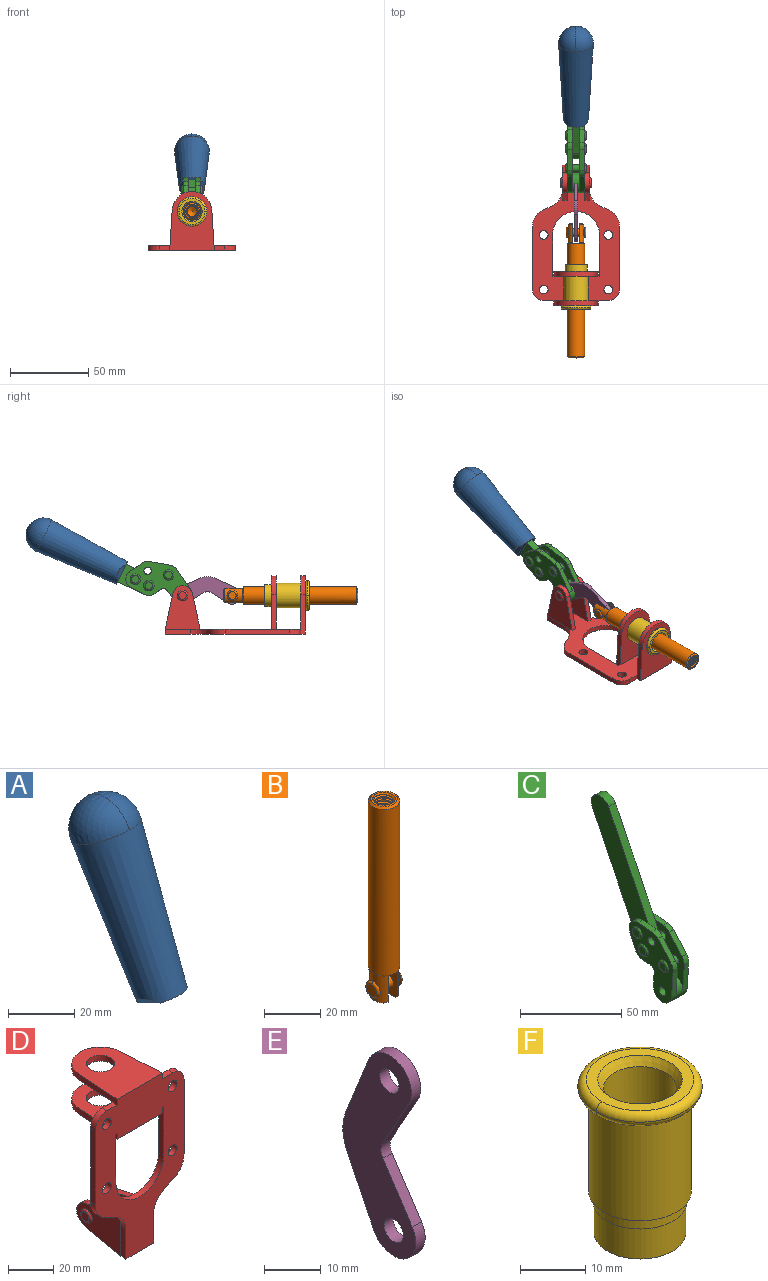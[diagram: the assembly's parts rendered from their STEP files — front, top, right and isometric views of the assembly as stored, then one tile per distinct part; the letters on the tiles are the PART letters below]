
ASSEMBLY  parts=6 mates=6
PART A: 11 faces, bbox 22.3x42.6x64.5 mm
  f0: sphere r=11.13mm, area 411.4mm2, adj f1,f8
  f1: cone r=11.11mm half-angle=3.3deg, axis (0,0.44,0.9), area 3251.8mm2, adj f0,f7,f8,f9,f10
  f2: cylinder r=6.16mm len=11.7mm, axis (1,0,0), area 89.5mm2, adj f3,f4,f5,f6
  f3: plane 60.23x36.75mm, normal (-1,0,0), area 763.6mm2, adj f2,f4,f6,f10
  f4: plane 51.37x25.05mm, normal (0,0.9,-0.44), area 264.2mm2, adj f2,f3,f5,f10
  f5: plane 60.23x36.75mm, normal (1,0,0), area 763.6mm2, adj f2,f4,f6,f10
  f6: plane 51.37x25.05mm, normal (0,-0.9,0.44), area 264.2mm2, adj f2,f3,f5,f10
  f7: plane 9.95x5.95mm, normal (0.71,-0.31,-0.64), area 25.8mm2, adj f1,f10
  f8: sphere r=11.13mm, area 411.4mm2, adj f0,f1
  f9: plane 9.95x5.95mm, normal (-0.71,-0.31,-0.64), area 25.8mm2, adj f1,f10
  f10: plane 14.27x11.38mm, normal (0,-0.44,-0.9), area 106.7mm2, adj f1,f3,f4,f5,f6,f7,f9
PART B: 48 faces, bbox 12.6x11.1x86.1 mm
  f0: torus R=2.41mm, axis (-1,0,0), area 15mm2, adj f30,f32,f34
  f1: torus R=2.41mm, axis (-1,0,0), area 15mm2, adj f29,f31,f33
  f2: cylinder r=5.54mm len=72.39mm, axis (0,0,1), area 2518.5mm2, adj f3,f4,f42,f43
  f3: cone r=5.54mm half-angle=45deg, axis (0,0,1), area 7.6mm2, adj f2,f5,f41
  f4: cone r=5.54mm half-angle=45deg, axis (0,0,-1), area 34.9mm2, adj f2,f39
  f5: cylinder r=5.08mm len=11.48mm, axis (0,0,1), area 108.3mm2, adj f3,f7,f8,f41
  f6: cylinder r=2.41mm len=4.83mm, axis (-1,0,0), area 71.2mm2, adj f40,f41
  f7: cylinder r=2.41mm len=4.83mm, axis (-1,0,0), area 7.6mm2, adj f5,f34
  f8: cone r=5.08mm half-angle=45deg, axis (0,0,1), area 10.6mm2, adj f5,f37,f41
  f9: cone r=3.98mm half-angle=45deg, axis (0,0,1), area 17.6mm2, adj f27,f39,f45,f46,f47
  f10: cylinder r=2.41mm len=4.83mm, axis (-1,0,0), area 7.6mm2, adj f33,f38
  f11: cylinder r=3.2mm len=6.4mm, axis (0,0,1), area 78.4mm2, adj f12,f28,f44,f45,f47
  f12: cylinder r=3.2mm len=6.4mm, axis (0,0,1), area 10.5mm2, adj f11,f13,f45,f47
  f13: cylinder r=3.2mm len=6.4mm, axis (0,0,1), area 10.5mm2, adj f12,f14,f45,f47
  f14: cylinder r=3.2mm len=6.4mm, axis (0,0,1), area 10.5mm2, adj f13,f15,f45,f47
  f15: cylinder r=3.2mm len=6.4mm, axis (0,0,1), area 10.5mm2, adj f14,f16,f45,f47
  f16: cylinder r=3.2mm len=6.4mm, axis (0,0,1), area 10.5mm2, adj f15,f17,f45,f47
  f17: cylinder r=3.2mm len=6.4mm, axis (0,0,1), area 10.5mm2, adj f16,f18,f45,f47
  f18: cylinder r=3.2mm len=6.4mm, axis (0,0,1), area 10.5mm2, adj f17,f19,f45,f47
  f19: cylinder r=3.2mm len=6.4mm, axis (0,0,1), area 10.5mm2, adj f18,f20,f45,f47
  f20: cylinder r=3.2mm len=6.4mm, axis (0,0,1), area 10.5mm2, adj f19,f21,f45,f47
  f21: cylinder r=3.2mm len=6.4mm, axis (0,0,1), area 10.5mm2, adj f20,f22,f45,f47
  f22: cylinder r=3.2mm len=6.4mm, axis (0,0,1), area 10.5mm2, adj f21,f23,f45,f47
  f23: cylinder r=3.2mm len=6.4mm, axis (0,0,1), area 10.5mm2, adj f22,f24,f45,f47
  f24: cylinder r=3.2mm len=6.4mm, axis (0,0,1), area 10.5mm2, adj f23,f25,f45,f47
  f25: cylinder r=3.2mm len=6.4mm, axis (0,0,1), area 10.5mm2, adj f24,f26,f45,f47
  f26: cylinder r=3.2mm len=6.4mm, axis (0,0,1), area 10.5mm2, adj f25,f27,f45,f47
  f27: cylinder r=3.2mm len=6.4mm, axis (0,0,1), area 7.4mm2, adj f9,f26,f45,f47
  f28: cone r=3.2mm half-angle=60deg, axis (0,0,1), area 37.2mm2, adj f11
  f29: plane 4.83x4.83mm, normal (-1,0,0), area 18.3mm2, adj f1,f31
  f30: plane 4.83x4.83mm, normal (1,0,0), area 18.3mm2, adj f0,f32
  f31: torus R=2.41mm, axis (-1,0,0), area 15mm2, adj f1,f29,f33
  f32: torus R=2.41mm, axis (-1,0,0), area 15mm2, adj f0,f30,f34
  f33: plane 6.83x6.83mm, normal (1,0,0), area 18.3mm2, adj f1,f10,f31
  f34: plane 6.83x6.83mm, normal (-1,0,0), area 18.3mm2, adj f0,f7,f32
  f35: cone r=5.08mm half-angle=45deg, axis (0,0,1), area 10.6mm2, adj f36,f38,f40
  f36: plane 7.25x1.97mm, normal (0,0,-1), area 10mm2, adj f35,f40
  f37: plane 7.25x1.97mm, normal (0,0,-1), area 10mm2, adj f8,f41
  f38: cylinder r=5.08mm len=11.48mm, axis (0,0,1), area 108.3mm2, adj f10,f35,f40,f42
  f39: plane 9.55x9.55mm, normal (0,0,1), area 22mm2, adj f4,f9
  f40: plane 12.76x10.09mm, normal (1,0,0), area 95.7mm2, adj f6,f35,f36,f38,f42,f43
  f41: plane 12.76x10.09mm, normal (-1,0,0), area 95.7mm2, adj f3,f5,f6,f8,f37,f43
  f42: cone r=5.54mm half-angle=45deg, axis (0,0,1), area 7.6mm2, adj f2,f38,f40
  f43: plane 11.07x4.7mm, normal (0,0,-1), area 50.4mm2, adj f2,f40,f41
  f44: plane 0.89x0.62mm, normal (-1,0,0), area 0.3mm2, adj f11,f45,f46,f47
  f45: bspline ~24.8x7.63mm, area 266.6mm2, adj f9,f11,f12,f13,f14,f15,f16,f17
  f46: bspline ~24.87x7.63mm, area 73.6mm2, adj f9,f44,f45,f47
  f47: bspline ~24.98x7.63mm, area 272.5mm2, adj f9,f11,f12,f13,f14,f15,f16,f17
PART C: 57 faces, bbox 12.9x60.2x99.6 mm
  f0: torus R=2.39mm, axis (-1,0,0), area 14.9mm2, adj f19,f41,f49
  f1: torus R=2.39mm, axis (-1,0,0), area 14.9mm2, adj f18,f40,f49
  f2: torus R=2.39mm, axis (-1,0,0), area 14.9mm2, adj f17,f33,f49
  f3: torus R=2.39mm, axis (-1,0,0), area 14.9mm2, adj f13,f16,f22
  f4: torus R=2.39mm, axis (-1,0,0), area 14.9mm2, adj f12,f15,f22
  f5: torus R=2.39mm, axis (-1,0,0), area 14.9mm2, adj f11,f14,f22
  f6: cylinder r=2.39mm len=4.78mm, axis (1,0,0), area 46.5mm2, adj f46,f48,f49
  f7: cylinder r=2.39mm len=10.9mm, axis (1,0,0), area 163.5mm2, adj f22,f49
  f8: cylinder r=6.35mm len=12.7mm, axis (1,0,0), area 311.1mm2, adj f22,f26,f27,f36,f37,f44,f48,f49
  f9: cylinder r=2.39mm len=4.78mm, axis (-1,0,0), area 70.5mm2, adj f44,f48
  f10: cylinder r=2.39mm len=4.78mm, axis (-1,0,0), area 46.5mm2, adj f22,f43,f44
  f11: plane 4.78x4.78mm, normal (1,0,0), area 17.9mm2, adj f5,f14
  f12: plane 4.78x4.78mm, normal (1,0,0), area 17.9mm2, adj f4,f15
  f13: plane 4.78x4.78mm, normal (1,0,0), area 17.9mm2, adj f3,f16
  f14: torus R=2.39mm, axis (-1,0,0), area 14.9mm2, adj f5,f11,f22
  f15: torus R=2.39mm, axis (-1,0,0), area 14.9mm2, adj f4,f12,f22
  f16: torus R=2.39mm, axis (-1,0,0), area 14.9mm2, adj f3,f13,f22
  f17: plane 4.78x4.78mm, normal (-1,0,0), area 17.9mm2, adj f2,f33
  f18: plane 4.78x4.78mm, normal (-1,0,0), area 17.9mm2, adj f1,f40
  f19: plane 4.78x4.78mm, normal (-1,0,0), area 17.9mm2, adj f0,f41
  f20: plane 2.26x0.2mm, normal (1,0,0), area 0.2mm2, adj f29,f42
  f21: plane 2.26x0.2mm, normal (-1,0,0), area 0.2mm2, adj f39,f42
  f22: plane 39.37x30.77mm, normal (1,0,0), area 565.5mm2, adj f3,f4,f5,f7,f8,f10,f14,f15
  f23: cylinder r=6.1mm len=4.15mm, axis (-1,0,0), area 14.7mm2, adj f22,f24,f30,f44
  f24: plane 10.25x9.01mm, normal (0,-0.75,0.66), area 42.3mm2, adj f22,f23,f25,f44
  f25: cylinder r=6.35mm len=4.64mm, axis (-1,0,0), area 15.6mm2, adj f22,f24,f26,f44
  f26: plane 15.84x3.1mm, normal (0,-1,-0.07), area 49.2mm2, adj f8,f22,f25,f44
  f27: plane 8.11x3.1mm, normal (0,1,0.07), area 25.2mm2, adj f8,f22,f28,f44
  f28: cylinder r=3.05mm len=3.25mm, axis (-1,0,0), area 14.8mm2, adj f22,f27,f29,f44
  f29: plane 5.99x3.1mm, normal (0,0.07,-1), area 18.6mm2, adj f20,f22,f28,f42,f44
  f30: plane 9.5x3.1mm, normal (0,-0.07,1), area 29.5mm2, adj f22,f23,f31,f44,f45
  f31: cylinder r=6.1mm len=8.63mm, axis (-1,0,0), area 39.1mm2, adj f22,f30,f32,f45
  f32: plane 8.65x3.96mm, normal (0,0.91,-0.42), area 29.5mm2, adj f22,f31,f42,f45
  f33: torus R=2.39mm, axis (-1,0,0), area 14.9mm2, adj f2,f17,f49
  f34: plane 10.25x9.01mm, normal (0,-0.75,0.66), area 42.3mm2, adj f35,f47,f48,f49
  f35: cylinder r=6.35mm len=4.64mm, axis (1,0,0), area 15.6mm2, adj f34,f36,f48,f49
  f36: plane 15.84x3.1mm, normal (0,-1,-0.07), area 49.2mm2, adj f8,f35,f48,f49
  f37: plane 8.11x3.1mm, normal (0,1,0.07), area 25.2mm2, adj f8,f38,f48,f49
  f38: cylinder r=3.05mm len=3.25mm, axis (1,0,0), area 14.8mm2, adj f37,f39,f48,f49
  f39: plane 5.99x3.1mm, normal (0,0.07,-1), area 18.6mm2, adj f21,f38,f42,f48,f49
  f40: torus R=2.39mm, axis (-1,0,0), area 14.9mm2, adj f1,f18,f49
  f41: torus R=2.39mm, axis (-1,0,0), area 14.9mm2, adj f0,f19,f49
  f42: cylinder r=6.35mm len=12.12mm, axis (-1,0,0), area 128.9mm2, adj f20,f21,f22,f29,f32,f39,f44,f45
  f43: plane 2.65x1.35mm, normal (1,0,0), area 1mm2, adj f10,f53
  f44: plane 33.18x20.42mm, normal (-1,0,0), area 303.8mm2, adj f8,f9,f10,f23,f24,f25,f26,f27
  f45: plane 77.62x39.82mm, normal (1,0,0), area 850mm2, adj f30,f31,f32,f42,f51,f52,f53
  f46: plane 2.65x1.35mm, normal (-1,0,0), area 1mm2, adj f6,f53
  f47: cylinder r=6.1mm len=4.15mm, axis (1,0,0), area 14.7mm2, adj f34,f48,f49,f54
  f48: plane 33.18x20.42mm, normal (1,0,0), area 303.8mm2, adj f6,f8,f9,f34,f35,f36,f37,f38
  f49: plane 39.37x30.77mm, normal (-1,0,0), area 565.5mm2, adj f0,f1,f2,f6,f7,f8,f33,f34
  f50: plane 8.65x3.96mm, normal (0,0.91,-0.42), area 29.5mm2, adj f42,f49,f55,f56
  f51: plane 68.49x33.4mm, normal (0,0.9,-0.44), area 358.1mm2, adj f42,f45,f52,f56
  f52: cylinder r=6.35mm len=12.06mm, axis (1,0,0), area 93.7mm2, adj f45,f51,f53,f56
  f53: plane 68.49x33.4mm, normal (0,-0.9,0.44), area 358.1mm2, adj f42,f43,f44,f45,f46,f48,f52,f56
  f54: plane 9.5x3.1mm, normal (0,-0.07,1), area 29.5mm2, adj f47,f48,f49,f55,f56
  f55: cylinder r=6.1mm len=8.63mm, axis (1,0,0), area 39.1mm2, adj f49,f50,f54,f56
  f56: plane 77.62x39.82mm, normal (-1,0,0), area 850mm2, adj f42,f50,f51,f52,f53,f54,f55
PART D: 55 faces, bbox 55.7x37.4x89.8 mm
  f0: torus R=2.41mm, axis (-1,0,0), area 15mm2, adj f11,f15,f25
  f1: torus R=2.41mm, axis (-1,0,0), area 15mm2, adj f10,f12,f22
  f2: cylinder r=2.78mm len=5.56mm, axis (0,-1,0), area 54.2mm2, adj f30,f54
  f3: cylinder r=14.99mm len=29.97mm, axis (0,-1,0), area 145.9mm2, adj f30,f49,f53,f54
  f4: cylinder r=2.78mm len=5.56mm, axis (0,-1,0), area 54.2mm2, adj f30,f54
  f5: cylinder r=2.78mm len=5.56mm, axis (0,-1,0), area 54.2mm2, adj f30,f54
  f6: cylinder r=2.78mm len=5.56mm, axis (0,-1,0), area 54.2mm2, adj f30,f54
  f7: cylinder r=6.35mm len=12.7mm, axis (0,0,1), area 123.6mm2, adj f27,f51
  f8: cylinder r=6.35mm len=12.7mm, axis (0,0,-1), area 124.7mm2, adj f21,f35
  f9: cylinder r=2.41mm len=11.18mm, axis (-1,0,0), area 169.4mm2, adj f16,f19
  f10: plane 4.83x4.83mm, normal (1,0,0), area 18.3mm2, adj f1,f12
  f11: plane 4.83x4.83mm, normal (-1,0,0), area 18.3mm2, adj f0,f15
  f12: torus R=2.41mm, axis (-1,0,0), area 15mm2, adj f1,f10,f22
  f13: cylinder r=6.35mm len=12.41mm, axis (1,0,0), area 53.4mm2, adj f18,f19,f22,f23
  f14: cylinder r=6.35mm len=12.41mm, axis (-1,0,0), area 53.4mm2, adj f16,f17,f24,f25
  f15: torus R=2.41mm, axis (-1,0,0), area 15mm2, adj f0,f11,f25
  f16: plane 27.86x22.35mm, normal (1,0,0), area 425.4mm2, adj f9,f14,f17,f24,f30
  f17: plane 22.86x4.97mm, normal (0,0.21,0.98), area 72.5mm2, adj f14,f16,f25,f30
  f18: plane 22.86x4.97mm, normal (0,0.21,0.98), area 72.5mm2, adj f13,f19,f22,f30
  f19: plane 27.86x22.35mm, normal (-1,0,0), area 425.4mm2, adj f9,f13,f18,f23,f30
  f20: cylinder r=12.7mm len=25.35mm, axis (0,0,-1), area 119.8mm2, adj f21,f34,f35,f36
  f21: plane 34.21x28.07mm, normal (0,0,-1), area 702.4mm2, adj f8,f20,f30,f34,f36
  f22: plane 27.96x22.45mm, normal (1,0,0), area 407.2mm2, adj f1,f12,f13,f18,f23,f30,f42,f43
  f23: plane 22.86x4.97mm, normal (0,0.21,-0.98), area 72.5mm2, adj f13,f19,f22,f44
  f24: plane 22.86x4.97mm, normal (0,0.21,-0.98), area 72.5mm2, adj f14,f16,f25,f44
  f25: plane 27.86x22.35mm, normal (-1,0,0), area 407.1mm2, adj f0,f14,f15,f17,f24,f30,f45,f46
  f26: plane 3.1x0.95mm, normal (0,0,-1), area 2.7mm2, adj f30,f49,f50,f54
  f27: plane 34.21x28.07mm, normal (0,0,1), area 702.4mm2, adj f7,f28,f30,f50,f52
  f28: cylinder r=12.7mm len=25.35mm, axis (0,0,1), area 118.8mm2, adj f27,f50,f51,f52
  f29: plane 3.1x0.95mm, normal (0,0,-1), area 2.7mm2, adj f30,f52,f53,f54
  f30: plane 86.54x55.63mm, normal (0,1,0), area 2362.9mm2, adj f2,f3,f4,f5,f6,f16,f17,f18
  f31: plane 40.56x3.1mm, normal (-1,0,0), area 125.7mm2, adj f30,f32,f48,f54
  f32: cylinder r=7.11mm len=7.11mm, axis (0,-1,0), area 34.6mm2, adj f30,f31,f33,f54
  f33: plane 6.67x3.1mm, normal (0,0,1), area 20.4mm2, adj f30,f32,f34,f54
  f34: plane 25.39x3.13mm, normal (-1,0.06,0), area 79.5mm2, adj f20,f21,f33,f35,f54
  f35: plane 37.31x28.45mm, normal (0,0,1), area 789.9mm2, adj f8,f20,f34,f36,f54
  f36: plane 25.39x3.13mm, normal (1,0.06,0), area 79.5mm2, adj f20,f21,f35,f37,f54
  f37: plane 6.67x3.1mm, normal (0,0,1), area 20.4mm2, adj f30,f36,f38,f54
  f38: cylinder r=7.11mm len=7.11mm, axis (0,-1,0), area 34.6mm2, adj f30,f37,f39,f54
  f39: plane 40.56x3.1mm, normal (1,0,0), area 125.7mm2, adj f30,f38,f40,f54
  f40: cylinder r=11.18mm len=10.16mm, axis (0,-1,0), area 39.5mm2, adj f30,f39,f41,f54
  f41: plane 6.09x3.1mm, normal (0.42,0,-0.91), area 20.8mm2, adj f30,f40,f42,f54
  f42: cylinder r=11.18mm len=9.41mm, axis (0,-1,0), area 37.2mm2, adj f22,f30,f41,f43,f54
  f43: plane 16.5x3.1mm, normal (1,0,0), area 51.1mm2, adj f22,f42,f44,f54
  f44: plane 17.37x3.1mm, normal (0,0,-1), area 53.8mm2, adj f23,f24,f30,f43,f45,f54
  f45: plane 16.5x3.1mm, normal (-1,0,0), area 51.1mm2, adj f25,f44,f46,f54
  f46: cylinder r=11.18mm len=9.41mm, axis (0,-1,0), area 37.2mm2, adj f25,f30,f45,f47,f54
  f47: plane 6.09x3.1mm, normal (-0.42,0,-0.91), area 20.8mm2, adj f30,f46,f48,f54
  f48: cylinder r=11.18mm len=10.16mm, axis (0,-1,0), area 39.5mm2, adj f30,f31,f47,f54
  f49: plane 26.54x3.1mm, normal (-1,0,0), area 82.3mm2, adj f3,f26,f30,f54
  f50: plane 25.39x3.1mm, normal (1,0.06,0), area 78.8mm2, adj f26,f27,f28,f51,f54
  f51: plane 37.31x28.45mm, normal (0,0,-1), area 789.9mm2, adj f7,f28,f50,f52,f54
  f52: plane 25.39x3.1mm, normal (-1,0.06,0), area 78.8mm2, adj f27,f28,f29,f51,f54
  f53: plane 26.54x3.1mm, normal (1,0,0), area 82.3mm2, adj f3,f29,f30,f54
  f54: plane 89.66x55.63mm, normal (0,-1,0), area 2678.5mm2, adj f2,f3,f4,f5,f6,f26,f29,f31
PART E: 12 faces, bbox 2.3x18.2x42.8 mm
  f0: cylinder r=2.4mm len=4.8mm, axis (1,0,0), area 34.9mm2, adj f4,f11
  f1: cylinder r=10.41mm len=8.47mm, axis (1,0,0), area 20.2mm2, adj f4,f9,f10,f11
  f2: cylinder r=3.05mm len=3.16mm, axis (1,0,0), area 7.7mm2, adj f4,f6,f7,f11
  f3: cylinder r=2.4mm len=4.8mm, axis (1,0,0), area 34.9mm2, adj f4,f11
  f4: plane 42.81x18.23mm, normal (-1,0,0), area 414.1mm2, adj f0,f1,f2,f3,f5,f6,f7,f8
  f5: cylinder r=5.54mm len=10.67mm, axis (1,0,0), area 41.8mm2, adj f4,f6,f10,f11
  f6: plane 11.66x6.53mm, normal (0,-0.87,-0.49), area 30.9mm2, adj f2,f4,f5,f11
  f7: plane 11.17x7.33mm, normal (0,-0.84,0.55), area 30.9mm2, adj f2,f4,f8,f11
  f8: cylinder r=5.54mm len=10.51mm, axis (1,0,0), area 41.8mm2, adj f4,f7,f9,f11
  f9: plane 13.67x6.67mm, normal (0,0.9,-0.44), area 35.1mm2, adj f1,f4,f8,f11
  f10: plane 14.1x5.7mm, normal (0,0.93,0.37), area 35.1mm2, adj f1,f4,f5,f11
  f11: plane 42.81x18.23mm, normal (1,0,0), area 414.1mm2, adj f0,f1,f2,f3,f5,f6,f7,f8
PART F: 15 faces, bbox 20.6x20.6x28.7 mm
  f0: torus R=8.26mm, axis (0,0,1), area 56.8mm2, adj f1,f10,f12
  f1: torus R=8.26mm, axis (0,0,1), area 56.8mm2, adj f0,f6,f13
  f2: cylinder r=5.59mm len=25.91mm, axis (0,0,1), area 909.6mm2, adj f3,f4
  f3: cone r=6.86mm half-angle=45deg, axis (0,0,-1), area 70.2mm2, adj f2,f14
  f4: cone r=6.47mm half-angle=30deg, axis (0,0,1), area 66.7mm2, adj f2,f13
  f5: cylinder r=7.04mm len=14.07mm, axis (0,0,1), area 252.6mm2, adj f11,f14
  f6: torus R=8.26mm, axis (0,0,1), area 56.8mm2, adj f1,f12,f13
  f7: cylinder r=7.16mm len=14.33mm, axis (0,0,1), area 91.5mm2, adj f9,f11
  f8: cylinder r=7.86mm len=18.42mm, axis (0,0,1), area 909.6mm2, adj f9,f10
  f9: plane 15.72x15.72mm, normal (0,0,-1), area 33mm2, adj f7,f8
  f10: plane 16.51x16.51mm, normal (0,0,-1), area 19.9mm2, adj f0,f8,f12
  f11: plane 14.33x14.33mm, normal (0,0,-1), area 5.7mm2, adj f5,f7
  f12: torus R=8.26mm, axis (0,0,1), area 56.8mm2, adj f0,f6,f10
  f13: plane 16.51x16.51mm, normal (0,0,1), area 82.7mm2, adj f1,f4,f6
  f14: plane 14.07x14.07mm, normal (0,0,-1), area 7.8mm2, adj f3,f5
PLACE A rot(axis=(-1,0,0),38.5deg) t=(-0.04,41.93,65.05)mm
PLACE B rot(axis=(1,0,0),90deg) t=(0,24.96,0)mm
PLACE C rot(axis=(-1,0,0),38.5deg) t=(0,41.93,65.05)mm
PLACE D rot(axis=(1,0,0),90deg) t=(0,9.14,0)mm fixed
PLACE E rot(axis=(1,0,0),92deg) t=(0,25.81,0.55)mm
PLACE F rot(axis=(1,0,0),90deg) t=(0,9.14,0)mm
MATE revolute C.f7 <-> D.f0  axis (1,0,0) through (0,41.23,24.61)mm
MATE revolute B.f6 <-> E.f5  axis (-1,0,0) through (0,9.48,24.61)mm
MATE fastened A.f2 <-> C.f52  axis (1,0,0) through (-2.35,131.62,63.75)mm
MATE revolute C.f7 <-> E.f3  axis (1,0,0) through (0,41.23,24.61)mm
MATE slider D.f7 <-> B.f2  axis (0,-1,0) through (0,-37.25,24.61)mm
MATE fastened F.f2 <-> D.f7  axis (0,-1,0) through (0,-37.25,24.61)mm
